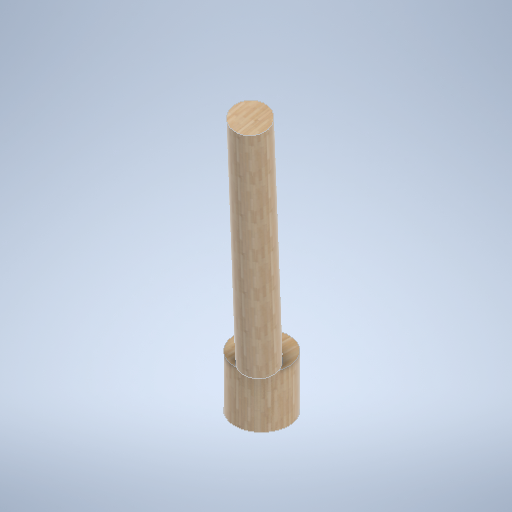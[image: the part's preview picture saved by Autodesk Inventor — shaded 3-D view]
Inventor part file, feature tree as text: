
AUTODESK INVENTOR PART (.ipt)
format: ipt  version: 2025 (Build 290162010, 162A)  size: 326,656 bytes
history: native  units: in
note: dims shown in document units (in); Inventor stores cm internally (conversion verified against a paired STEP export)
features: sketch x4, plane x2, extrude x1, revolve x1
ambient origin geometry x8: Origin, YZ Plane, XZ Plane, XY Plane, X Axis, Y Axis, Z Axis, Center Point
bodies: Solid1 (feature_tree)
feature tree (8):
  extrude  "Extrusion1"  Depth=48.0in TaperAngle=0.0deg
  plane  "Work Plane3"
  sketch  "Sketch2"  dims[d3=34.0in d6=12.0in]
  plane  "Work Plane5"
  sketch  "Sketch4"  dims[d8=44.0in d9=48.0in d10=4.0in d11=27.5in d13=240.0in d14=90.0deg]
  revolve  "Revolution1"  [1 undecoded]
  sketch  "Sketch1"  dims[d0=50.0in d1=48.0in d2=0.0in]
  sketch  "Sketch3"  dims[d7=90.0deg]
note: 1 required parameter value undecoded (feature->parameter linkage not recoverable at this tier; creation-order binding heuristic only, values carry confidence <= 0.55)
